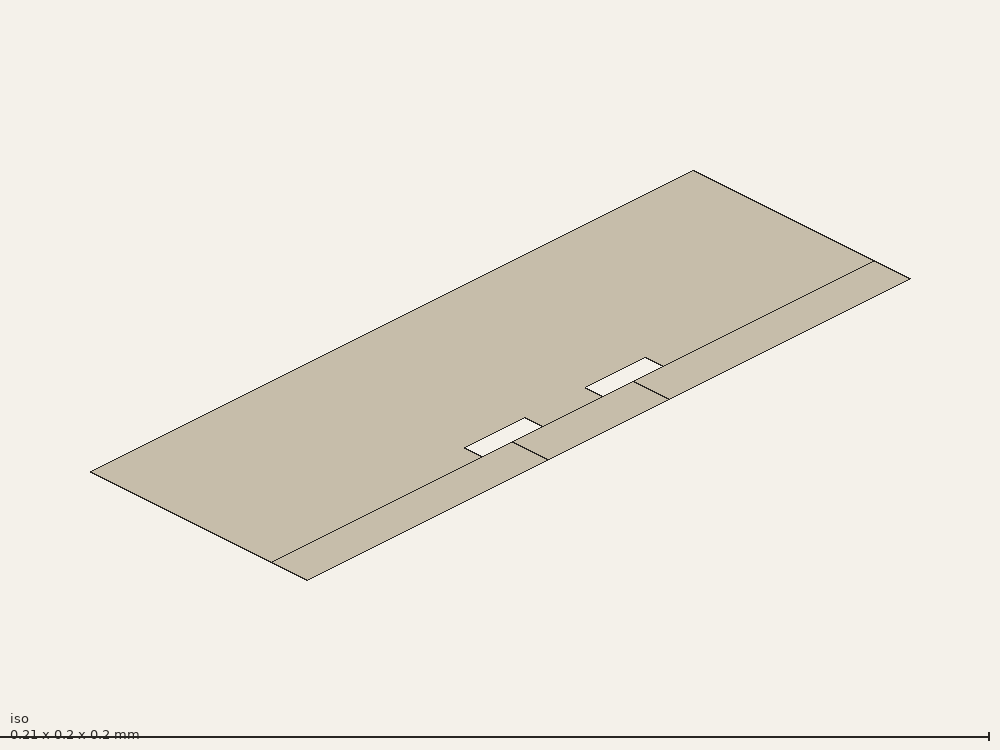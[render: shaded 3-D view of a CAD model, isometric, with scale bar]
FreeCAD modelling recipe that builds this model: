
FCSTD DOCUMENT  (FreeCAD 0.21R33694 (Git))
Label: coupled_microstrip
License: All rights reserved
LicenseURL: http://en.wikipedia.org/wiki/All_rights_reserved
objects: Part::Part2DObjectPython×8, App::FeaturePython×4, Part::Cut×2, Part::FeaturePython×1
note: 11 computed .brp shape members not serialized (recipe doc carries the construction recipe); baked Part::Feature solids carry a one-line shape summary decoded from their .brp

FEATURE [Part::Part2DObjectPython] Rectangle  label="cut1"  # Draft 2D object (typed FeaturePython)
  Area = 3e-07
  ChamferSize = 0
  Columns = 1
  FilletRadius = 0
  Height = 0.0003
  Length = 0.001
  MakeFace = true
  Placement = pos=(-0.0015,0,0) rot=(0,0,1;0rad)
  Rows = 1
FEATURE [Part::Part2DObjectPython] Rectangle001  label="_Pi1"  # Draft 2D object (typed FeaturePython)
  Area = 3e-07
  ChamferSize = 0
  Columns = 1
  FilletRadius = 0
  Height = 0.0003
  Length = 0.001
  MakeFace = true
  Placement = pos=(-0.0015,0,0) rot=(0,0,1;0rad)
  Rows = 1
FEATURE [Part::Part2DObjectPython] Rectangle002  label="cut2"  # Draft 2D object (typed FeaturePython)
  Area = 3e-07
  ChamferSize = 0
  Columns = 1
  FilletRadius = 0
  Height = 0.0003
  Length = 0.001
  MakeFace = true
  Placement = pos=(0.0005,0,0) rot=(0,0,1;0rad)
  Rows = 1
FEATURE [Part::Part2DObjectPython] Rectangle003  label="_Pi2"  # Draft 2D object (typed FeaturePython)
  Area = 3e-07
  ChamferSize = 0
  Columns = 1
  FilletRadius = 0
  Height = 0.0003
  Length = 0.001
  MakeFace = true
  Placement = pos=(0.0005,0,0) rot=(0,0,1;0rad)
  Rows = 1
FEATURE [Part::Part2DObjectPython] Rectangle004  label="substrate"  # Draft 2D object (typed FeaturePython)
  Area = 6.35e-06
  ChamferSize = 0
  Columns = 1
  FilletRadius = 0
  Height = 0.000635
  Length = 0.01
  MakeFace = true
  Placement = pos=(-0.005,-0.000635,0) rot=(0,0,1;0rad)
  Rows = 1
FEATURE [Part::Part2DObjectPython] Rectangle005  label="air"  # Draft 2D object (typed FeaturePython)
  Area = 3e-05
  ChamferSize = 0
  Columns = 1
  FilletRadius = 0
  Height = 0.003
  Length = 0.01
  MakeFace = true
  Placement = pos=(-0.005,0,0) rot=(0,0,1;0rad)
  Rows = 1
FEATURE [Part::Cut] Cut
  Base = -> Rectangle005
  Tool = -> Rectangle
FEATURE [Part::Cut] Cut001  label="air-metal"
  Base = -> Cut
  Tool = -> Rectangle002
FEATURE [Part::Part2DObjectPython] Line  label="_Pv1"  # Draft 2D object (typed FeaturePython)
  Area = 0
  ChamferSize = 0
  Closed = false
  End = (-0.001,0,0)
  FilletRadius = 0
  Length = 0.000635
  MakeFace = true
  Placement = pos=(-0.001,-0.000635,0) rot=(0,0,1;0rad)
  Points = (2) [(0,0,0),(3.88825e-20,0.000635,0)]
  Start = (-0.001,-0.000635,0)
  Subdivisions = 0
FEATURE [Part::Part2DObjectPython] Line001  label="_Pv2"  # Draft 2D object (typed FeaturePython)
  Area = 0
  ChamferSize = 0
  Closed = false
  End = (0.001,0,0)
  FilletRadius = 0
  Length = 0.000635
  MakeFace = true
  Placement = pos=(0.001,-0.000635,0) rot=(0,0,1;0rad)
  Points = (2) [(0,0,0),(3.88825e-20,0.000635,0)]
  Start = (0.001,-0.000635,0)
  Subdivisions = 0
FEATURE [App::FeaturePython] Text  label="_L1(voltage){v1}"  # WARN: FeaturePython — macro-defined, semantics opaque (R4)
  Placement = pos=(-0.0314219,-0.0122714,0) rot=(0,0,1;0rad)
  Text = .
FEATURE [App::FeaturePython] Text001  label="_L2(voltage){v2}"  # WARN: FeaturePython — macro-defined, semantics opaque (R4)
  Placement = pos=(-0.0314219,-0.0122714,0) rot=(0,0,1;0rad)
  Text = .
FEATURE [App::FeaturePython] Text002  label="_L1(current){i1}"  # WARN: FeaturePython — macro-defined, semantics opaque (R4)
  Placement = pos=(-0.0314219,-0.0122714,0) rot=(0,0,1;0rad)
  Text = .
FEATURE [App::FeaturePython] Text003  label="_L2(current){i2}"  # WARN: FeaturePython — macro-defined, semantics opaque (R4)
  Placement = pos=(-0.0314219,-0.0122714,0) rot=(0,0,1;0rad)
  Text = .
FEATURE [Part::FeaturePython] BooleanFragments  # WARN: FeaturePython — macro-defined, semantics opaque (R4)
  Mode = 0
  Objects = -> [Rectangle004,Cut001,Line,Line001]
  Tolerance = 0
